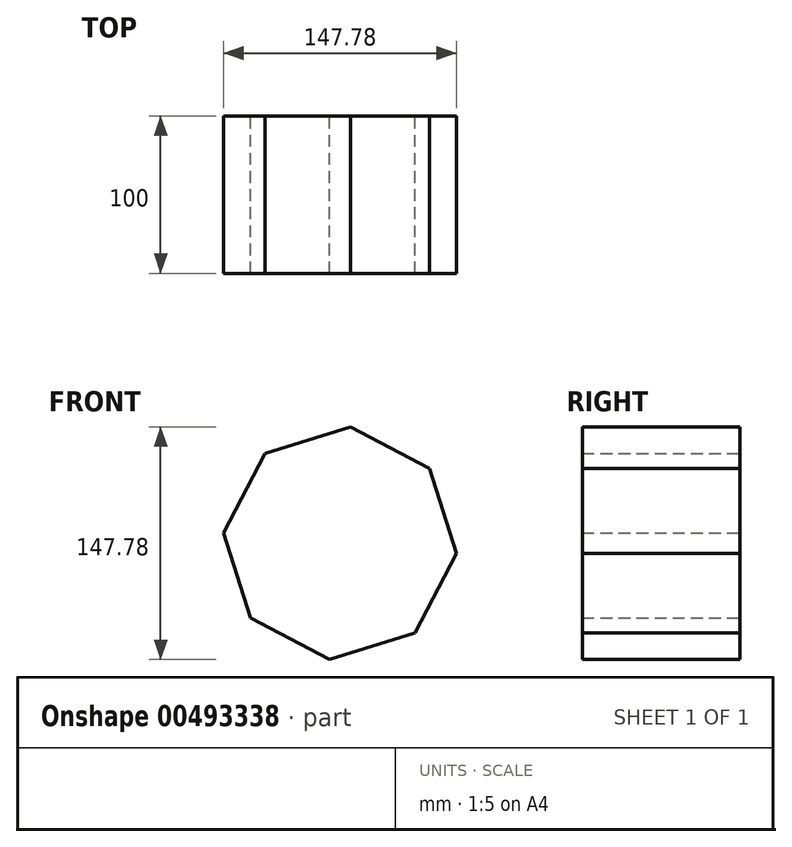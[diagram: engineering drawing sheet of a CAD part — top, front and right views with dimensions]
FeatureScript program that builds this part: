
annotation { "Feature Type Name" : "Feature", "Feature Type Description" : "" }
export const myFeature = defineFeature(function(context is Context, id is Id, definition is map)
    precondition{}
    {
        {
            var Q0;
            Q0=qCreatedBy(makeId("Front.planeOp"),FACE);
            var sketch = newSketch(context, id + "F0", { "sketchPlane" : qUnion([Q0])});
            skCircle(sketch, "E0.cCircle", {"center": v(0, 0) * mm, "radius": 74.2 * mm, "construction": true});
            skLineSegment(sketch, "E0.0", {"start": v(-73.9, 6.64) * mm, "end": v(-47.56, 56.94) * mm});
            skLineSegment(sketch, "E0.1", {"start": v(-47.56, 56.94) * mm, "end": v(6.64, 73.9) * mm});
            skLineSegment(sketch, "E0.2", {"start": v(6.64, 73.9) * mm, "end": v(56.94, 47.56) * mm});
            skLineSegment(sketch, "E0.3", {"start": v(56.94, 47.56) * mm, "end": v(73.9, -6.64) * mm});
            skLineSegment(sketch, "E0.4", {"start": v(73.9, -6.64) * mm, "end": v(47.56, -56.94) * mm});
            skLineSegment(sketch, "E0.5", {"start": v(47.56, -56.94) * mm, "end": v(-6.64, -73.9) * mm});
            skLineSegment(sketch, "E0.6", {"start": v(-6.64, -73.9) * mm, "end": v(-56.94, -47.56) * mm});
            skLineSegment(sketch, "E0.7", {"start": v(-56.94, -47.56) * mm, "end": v(-73.9, 6.64) * mm});
            skSolve(sketch);
        }
        {
            var Q0;
            Q0=makeQuery(id+"F0.imprint","IMPRINT",FACE,{"disambiguationData":[TD([[makeQuery(id+"F0.imprint","IMPRINT",EDGE,{"derivedFrom":sQuery(id+"F0.wireOp",EDGE,"E0.0")}),-1.0]])]});
            extrude(context, id + "F1", {"entities" : qUnion([Q0]), "depth" : 100 * mm});
        }
    });
